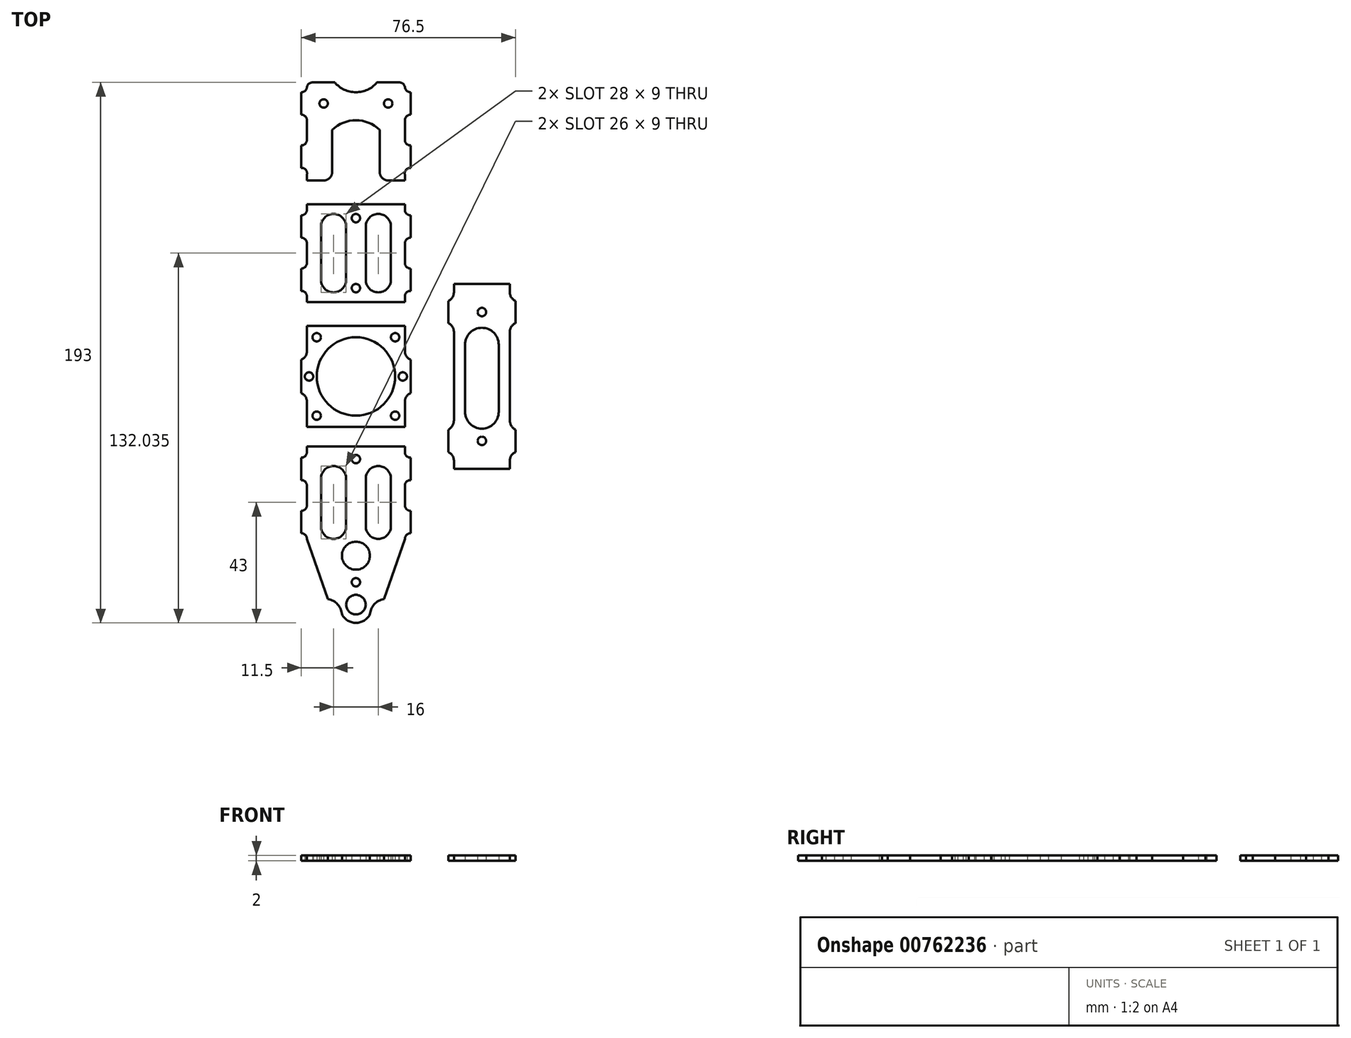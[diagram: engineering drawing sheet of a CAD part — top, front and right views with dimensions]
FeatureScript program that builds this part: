
annotation { "Feature Type Name" : "Feature", "Feature Type Description" : "" }
export const myFeature = defineFeature(function(context is Context, id is Id, definition is map)
    precondition{}
    {
        {
            var Q0;
            Q0=qCreatedBy(makeId("Top.planeOp"),FACE);
            var sketch = newSketch(context, id + "F0", { "sketchPlane" : qUnion([Q0])});
            skCircle(sketch, "E0", {"center": v(0, 0) * mm, "radius": 14 * mm});
            skCircle(sketch, "E1", {"center": v(-16.75, 0) * mm, "radius": 1.5 * mm});
            skLineSegment(sketch, "E2", {"start": v(-17.5, 18) * mm, "end": v(17.5, 18) * mm});
            skLineSegment(sketch, "E3.MirrorCS", {"start": v(-17.5, -18) * mm, "end": v(17.5, -18) * mm});
            skLineSegment(sketch, "E4", {"start": v(-17.5, 18) * mm, "end": v(-17.5, 9) * mm});
            skLineSegment(sketch, "E5", {"start": v(-19.5, 6) * mm, "end": v(-19.5, -6) * mm});
            skLineSegment(sketch, "E6.MirrorCS", {"start": v(-17.5, -18) * mm, "end": v(-17.5, -9) * mm});
            skLineSegment(sketch, "E7.MirrorCS", {"start": v(17.5, -18) * mm, "end": v(17.5, -9) * mm});
            skCircle(sketch, "E8.MirrorC", {"center": v(16.75, 0) * mm, "radius": 1.5 * mm});
            skLineSegment(sketch, "E9.MirrorCS", {"start": v(17.5, 18) * mm, "end": v(17.5, 9) * mm});
            skLineSegment(sketch, "E10.MirrorCS", {"start": v(19.5, 6) * mm, "end": v(19.5, -6) * mm});
            skCircle(sketch, "E11", {"center": v(-14, 14) * mm, "radius": 1.5 * mm});
            skCircle(sketch, "E12.MirrorC", {"center": v(-14, -14) * mm, "radius": 1.5 * mm});
            skCircle(sketch, "E13.MirrorC", {"center": v(14, 14) * mm, "radius": 1.5 * mm});
            skCircle(sketch, "E14.MirrorC", {"center": v(14, -14) * mm, "radius": 1.5 * mm});
            skArc(sketch, "E15", {"start": v(-19.5, 6) * mm, "mid": v(-18.05, 7.2) * mm, "end": v(-17.5, 9) * mm});
            skArc(sketch, "E16", {"start": v(17.5, 9) * mm, "mid": v(18.05, 7.2) * mm, "end": v(19.5, 6) * mm});
            skArc(sketch, "E17", {"start": v(-17.5, -9) * mm, "mid": v(-18.05, -7.2) * mm, "end": v(-19.5, -6) * mm});
            skArc(sketch, "E18", {"start": v(19.5, -6) * mm, "mid": v(18.05, -7.2) * mm, "end": v(17.5, -9) * mm});
            skSolve(sketch);
        }
        {
            var Q0;
            Q0 = qSketchRegion(id + "F0", true);
            extrude(context, id + "F1", {"entities" : qUnion([Q0]), "depth" : 2 * mm, "offsetDistance" : 25 * mm});
        }
        {
            var Q0;
            Q0=qCreatedBy(makeId("Top.planeOp"),FACE);
            var sketch = newSketch(context, id + "F2", { "sketchPlane" : qUnion([Q0])});
            skLineSegment(sketch, "E19", {"start": v(-17.5, 47.53) * mm, "end": v(-17.5, 40.53) * mm});
            skLineSegment(sketch, "E20", {"start": v(-17.5, 61.53) * mm, "end": v(17.5, 61.53) * mm});
            skPoint(sketch, "E21.positionSnap0", {"position": v(0, 61.53) * mm});
            skLineSegment(sketch, "E22", {"start": v(-17.5, 61.53) * mm, "end": v(-17.5, 59.53) * mm});
            skLineSegment(sketch, "E23", {"start": v(17.5, 47.53) * mm, "end": v(17.5, 40.53) * mm});
            skLineSegment(sketch, "E24", {"start": v(-17.5, 26.53) * mm, "end": v(17.5, 26.53) * mm});
            skPoint(sketch, "E25", {"position": v(0, 26.53) * mm});
            skLineSegment(sketch, "E26", {"start": v(-17.5, 28.53) * mm, "end": v(-17.5, 26.53) * mm});
            skLineSegment(sketch, "E27", {"start": v(-19.5, 57.53) * mm, "end": v(-19.5, 49.53) * mm});
            skLineSegment(sketch, "E28.MirrorCS", {"start": v(19.5, 57.53) * mm, "end": v(19.5, 49.53) * mm});
            skLineSegment(sketch, "E29", {"start": v(-19.5, 38.53) * mm, "end": v(-19.5, 30.53) * mm});
            skLineSegment(sketch, "E30", {"start": v(0, 61.53) * mm, "end": v(0, 26.53) * mm, "construction": true});
            skPoint(sketch, "E31", {"position": v(0, 44.03) * mm});
            skPoint(sketch, "E32", {"position": v(-17.5, 44.03) * mm});
            skPoint(sketch, "E33", {"position": v(17.5, 44.03) * mm});
            skLineSegment(sketch, "E34.MirrorCS", {"start": v(19.5, 38.53) * mm, "end": v(19.5, 30.53) * mm});
            skLineSegment(sketch, "E35", {"start": v(-17.5, 44.03) * mm, "end": v(17.5, 44.03) * mm, "construction": true});
            skLineSegment(sketch, "E36.MirrorCS", {"start": v(17.5, 61.53) * mm, "end": v(17.5, 59.53) * mm});
            skLineSegment(sketch, "E37.MirrorCS", {"start": v(17.5, 28.53) * mm, "end": v(17.5, 26.53) * mm});
            skArc(sketch, "E38", {"start": v(-17.5, 59.53) * mm, "mid": v(-18.09, 58.12) * mm, "end": v(-19.5, 57.53) * mm});
            skArc(sketch, "E39", {"start": v(-17.5, 47.53) * mm, "mid": v(-18.09, 48.95) * mm, "end": v(-19.5, 49.53) * mm});
            skArc(sketch, "E40.MirrorCS", {"start": v(-17.5, 28.53) * mm, "mid": v(-18.09, 29.95) * mm, "end": v(-19.5, 30.53) * mm});
            skArc(sketch, "E41.MirrorCS", {"start": v(-17.5, 40.53) * mm, "mid": v(-18.09, 39.12) * mm, "end": v(-19.5, 38.53) * mm});
            skArc(sketch, "E42.MirrorCS", {"start": v(17.5, 59.53) * mm, "mid": v(18.09, 58.12) * mm, "end": v(19.5, 57.53) * mm});
            skArc(sketch, "E43.MirrorCS", {"start": v(17.5, 47.53) * mm, "mid": v(18.09, 48.95) * mm, "end": v(19.5, 49.53) * mm});
            skArc(sketch, "E44.MirrorCS", {"start": v(17.5, 40.53) * mm, "mid": v(18.09, 39.12) * mm, "end": v(19.5, 38.53) * mm});
            skArc(sketch, "E45.MirrorCS", {"start": v(17.5, 28.53) * mm, "mid": v(18.09, 29.95) * mm, "end": v(19.5, 30.53) * mm});
            skLineSegment(sketch, "E46.top", {"start": v(-12.5, 34.53) * mm, "end": v(-3.5, 34.53) * mm, "construction": true});
            skLineSegment(sketch, "E46.left", {"start": v(-12.5, 53.53) * mm, "end": v(-12.5, 34.53) * mm});
            skLineSegment(sketch, "E46.right", {"start": v(-3.5, 53.53) * mm, "end": v(-3.5, 34.53) * mm});
            skArc(sketch, "E47", {"start": v(-3.5, 53.53) * mm, "mid": v(-8, 58.03) * mm, "end": v(-12.5, 53.53) * mm});
            skArc(sketch, "E48", {"start": v(-12.5, 34.53) * mm, "mid": v(-8, 30.03) * mm, "end": v(-3.5, 34.53) * mm});
            skLineSegment(sketch, "E49", {"start": v(-12.5, 53.53) * mm, "end": v(-3.5, 53.53) * mm, "construction": true});
            skLineSegment(sketch, "E50.MirrorCS", {"start": v(12.5, 34.53) * mm, "end": v(3.5, 34.53) * mm, "construction": true});
            skLineSegment(sketch, "E51.MirrorCS", {"start": v(12.5, 53.53) * mm, "end": v(3.5, 53.53) * mm, "construction": true});
            skArc(sketch, "E52.MirrorCS", {"start": v(12.5, 34.53) * mm, "mid": v(8, 30.03) * mm, "end": v(3.5, 34.53) * mm});
            skLineSegment(sketch, "E53.MirrorCS", {"start": v(12.5, 53.53) * mm, "end": v(12.5, 34.53) * mm});
            skLineSegment(sketch, "E54.MirrorCS", {"start": v(3.5, 53.53) * mm, "end": v(3.5, 34.53) * mm});
            skArc(sketch, "E55.MirrorCS", {"start": v(3.5, 53.53) * mm, "mid": v(8, 58.03) * mm, "end": v(12.5, 53.53) * mm});
            skPoint(sketch, "E56", {"position": v(-8, 58.03) * mm});
            skPoint(sketch, "E57", {"position": v(8, 58.03) * mm});
            skLineSegment(sketch, "E58", {"start": v(-8, 58.03) * mm, "end": v(8, 58.03) * mm, "construction": true});
            skCircle(sketch, "E59", {"center": v(0, 56.53) * mm, "radius": 1.5 * mm});
            skPoint(sketch, "E60", {"position": v(0, 58.03) * mm});
            skCircle(sketch, "E61.MirrorC", {"center": v(0, 31.53) * mm, "radius": 1.5 * mm});
            skSolve(sketch);
        }
        {
            var Q0;
            Q0 = qSketchRegion(id + "F2", true);
            extrude(context, id + "F3", {"entities" : qUnion([Q0]), "depth" : 2 * mm, "offsetDistance" : 25 * mm});
        }
        {
            var Q0;
            Q0=qCreatedBy(makeId("Top.planeOp"),FACE);
            var sketch = newSketch(context, id + "F4", { "sketchPlane" : qUnion([Q0])});
            skLineSegment(sketch, "E62", {"start": v(-17.5, 70) * mm, "end": v(-11.53, 70) * mm});
            skLineSegment(sketch, "E63", {"start": v(-17.5, 91.5) * mm, "end": v(-17.5, 84.5) * mm});
            skPoint(sketch, "E64", {"position": v(-17.5, 88) * mm});
            skLineSegment(sketch, "E65.MirrorCS", {"start": v(17.5, 91.5) * mm, "end": v(17.5, 84.5) * mm});
            skLineSegment(sketch, "E66", {"start": v(-17.5, 70) * mm, "end": v(-17.5, 72) * mm});
            skLineSegment(sketch, "E67.MirrorCS", {"start": v(17.5, 70) * mm, "end": v(11.53, 70) * mm});
            skLineSegment(sketch, "E68.MirrorCS", {"start": v(17.5, 70) * mm, "end": v(17.5, 72) * mm});
            skLineSegment(sketch, "E69", {"start": v(-8.5, 88) * mm, "end": v(-8.5, 73) * mm});
            skLineSegment(sketch, "E70.MirrorCS", {"start": v(8.5, 88) * mm, "end": v(8.5, 73) * mm});
            skArc(sketch, "E71", {"start": v(8.5, 88) * mm, "mid": v(0, 91.5) * mm, "end": v(-8.5, 88) * mm});
            skPoint(sketch, "E72", {"position": v(0, 91.5) * mm});
            skLineSegment(sketch, "E73", {"start": v(-15.53, 105) * mm, "end": v(-7.53, 105) * mm});
            skLineSegment(sketch, "E74", {"start": v(-17.52, 105) * mm, "end": v(-17.52, 101.5) * mm, "construction": true});
            skLineSegment(sketch, "E75.MirrorCS", {"start": v(15.53, 105) * mm, "end": v(7.53, 105) * mm});
            skLineSegment(sketch, "E76", {"start": v(-19.5, 101.5) * mm, "end": v(-19.5, 93.5) * mm});
            skLineSegment(sketch, "E77", {"start": v(-17.5, 88) * mm, "end": v(17.5, 88) * mm, "construction": true});
            skLineSegment(sketch, "E78.MirrorCS", {"start": v(-19.5, 74.5) * mm, "end": v(-19.5, 82.5) * mm});
            skArc(sketch, "E79", {"start": v(-17.5, 91.5) * mm, "mid": v(-18.09, 92.91) * mm, "end": v(-19.5, 93.5) * mm});
            skArc(sketch, "E80.MirrorCS", {"start": v(-17.5, 84.5) * mm, "mid": v(-18.09, 83.09) * mm, "end": v(-19.5, 82.5) * mm});
            skLineSegment(sketch, "E81", {"start": v(-19.5, 101.5) * mm, "end": v(-17.52, 101.5) * mm, "construction": true});
            skLineSegment(sketch, "E82", {"start": v(-17.52, 101.5) * mm, "end": v(-17.5, 70) * mm, "construction": true});
            skPoint(sketch, "E83", {"position": v(-17.52, 103.25) * mm});
            skArc(sketch, "E84", {"start": v(-19.5, 101.5) * mm, "mid": v(-18.18, 102) * mm, "end": v(-17.52, 103.25) * mm});
            skArc(sketch, "E85", {"start": v(-15.53, 105) * mm, "mid": v(-16.86, 104.5) * mm, "end": v(-17.52, 103.25) * mm});
            skLineSegment(sketch, "E86", {"start": v(0, 105) * mm, "end": v(0, 79.43) * mm, "construction": true});
            skPoint(sketch, "E87", {"position": v(0, 101.5) * mm});
            skArc(sketch, "E88", {"start": v(-7.53, 105) * mm, "mid": v(0, 101.5) * mm, "end": v(7.53, 105) * mm});
            skArc(sketch, "E89", {"start": v(-17.5, 72) * mm, "mid": v(-17.87, 73.75) * mm, "end": v(-19.5, 74.5) * mm});
            skPoint(sketch, "E90", {"position": v(-11.53, 105) * mm});
            skArc(sketch, "E91", {"start": v(-11.53, 70) * mm, "mid": v(-9.4, 70.87) * mm, "end": v(-8.5, 73) * mm});
            skArc(sketch, "E92.MirrorCS", {"start": v(11.53, 70) * mm, "mid": v(9.4, 70.87) * mm, "end": v(8.5, 73) * mm});
            skLineSegment(sketch, "E93.MirrorCS", {"start": v(19.5, 74.5) * mm, "end": v(19.5, 82.5) * mm});
            skLineSegment(sketch, "E94.MirrorCS", {"start": v(19.5, 101.5) * mm, "end": v(19.5, 93.5) * mm});
            skArc(sketch, "E95.MirrorCS", {"start": v(15.53, 105) * mm, "mid": v(16.86, 104.5) * mm, "end": v(17.52, 103.25) * mm});
            skArc(sketch, "E96.MirrorCS", {"start": v(19.5, 101.5) * mm, "mid": v(18.18, 102) * mm, "end": v(17.52, 103.25) * mm});
            skArc(sketch, "E97.MirrorCS", {"start": v(17.5, 91.5) * mm, "mid": v(18.09, 92.91) * mm, "end": v(19.5, 93.5) * mm});
            skArc(sketch, "E98.MirrorCS", {"start": v(17.5, 84.5) * mm, "mid": v(18.09, 83.09) * mm, "end": v(19.5, 82.5) * mm});
            skArc(sketch, "E99.MirrorCS", {"start": v(17.5, 72) * mm, "mid": v(17.87, 73.75) * mm, "end": v(19.5, 74.5) * mm});
            skPoint(sketch, "E100", {"position": v(-19.5, 97.5) * mm});
            skPoint(sketch, "E101.MirrorP", {"position": v(19.5, 97.5) * mm});
            skCircle(sketch, "E102", {"center": v(-11.53, 97.5) * mm, "radius": 1.5 * mm});
            skCircle(sketch, "E103.MirrorC", {"center": v(11.53, 97.5) * mm, "radius": 1.5 * mm});
            skSolve(sketch);
        }
        {
            var Q0;
            Q0 = qSketchRegion(id + "F4", true);
            extrude(context, id + "F5", {"entities" : qUnion([Q0]), "depth" : 2 * mm, "offsetDistance" : 25 * mm});
        }
        {
            var Q0;
            Q0=qCreatedBy(makeId("Top.planeOp"),FACE);
            var sketch = newSketch(context, id + "F6", { "sketchPlane" : qUnion([Q0])});
            skLineSegment(sketch, "E104", {"start": v(-17.5, -25) * mm, "end": v(17.5, -25) * mm});
            skPoint(sketch, "E105", {"position": v(0, -25) * mm});
            skCircle(sketch, "E106", {"center": v(0, -29.5) * mm, "radius": 1.5 * mm});
            skCircle(sketch, "E107", {"center": v(0, -64) * mm, "radius": 5 * mm});
            skCircle(sketch, "E108", {"center": v(0, -73.5) * mm, "radius": 1.5 * mm});
            skCircle(sketch, "E109", {"center": v(0, -81.5) * mm, "radius": 3.5 * mm});
            skPoint(sketch, "E110", {"position": v(0, -88) * mm});
            skPoint(sketch, "E111", {"position": v(0, -85) * mm});
            skLineSegment(sketch, "E112", {"start": v(-5, -85) * mm, "end": v(5, -85) * mm, "construction": true});
            skLineSegment(sketch, "E113", {"start": v(-10, -81.5) * mm, "end": v(10, -81.5) * mm, "construction": true});
            skLineSegment(sketch, "E114", {"start": v(-19.5, -29) * mm, "end": v(-19.5, -37) * mm});
            skLineSegment(sketch, "E115", {"start": v(-17.5, -25) * mm, "end": v(-17.5, -27) * mm});
            skArc(sketch, "E116", {"start": v(-19.5, -29) * mm, "mid": v(-18.09, -28.41) * mm, "end": v(-17.5, -27) * mm});
            skLineSegment(sketch, "E117", {"start": v(-17.5, -39) * mm, "end": v(-17.5, -46) * mm});
            skArc(sketch, "E118", {"start": v(-17.5, -39) * mm, "mid": v(-18.09, -37.59) * mm, "end": v(-19.5, -37) * mm});
            skPoint(sketch, "E119", {"position": v(-17.5, -42.5) * mm});
            skLineSegment(sketch, "E120", {"start": v(-17.5, -42.5) * mm, "end": v(17.5, -42.5) * mm, "construction": true});
            skLineSegment(sketch, "E121.MirrorCS", {"start": v(-19.5, -56) * mm, "end": v(-19.5, -48) * mm});
            skArc(sketch, "E122.MirrorCS", {"start": v(-19.5, -56) * mm, "mid": v(-18.09, -56.59) * mm, "end": v(-17.5, -58) * mm});
            skArc(sketch, "E123.MirrorCS", {"start": v(-17.5, -46) * mm, "mid": v(-18.09, -47.41) * mm, "end": v(-19.5, -48) * mm});
            skLineSegment(sketch, "E124.MirrorCS", {"start": v(17.5, -25) * mm, "end": v(17.5, -27) * mm});
            skArc(sketch, "E125.MirrorCS", {"start": v(19.5, -29) * mm, "mid": v(18.09, -28.41) * mm, "end": v(17.5, -27) * mm});
            skLineSegment(sketch, "E126.MirrorCS", {"start": v(19.5, -29) * mm, "end": v(19.5, -37) * mm});
            skArc(sketch, "E127.MirrorCS", {"start": v(17.5, -39) * mm, "mid": v(18.09, -37.59) * mm, "end": v(19.5, -37) * mm});
            skLineSegment(sketch, "E128.MirrorCS", {"start": v(17.5, -39) * mm, "end": v(17.5, -46) * mm});
            skArc(sketch, "E129.MirrorCS", {"start": v(17.5, -46) * mm, "mid": v(18.09, -47.41) * mm, "end": v(19.5, -48) * mm});
            skLineSegment(sketch, "E130.MirrorCS", {"start": v(19.5, -56) * mm, "end": v(19.5, -48) * mm});
            skArc(sketch, "E131.MirrorCS", {"start": v(19.5, -56) * mm, "mid": v(18.09, -56.59) * mm, "end": v(17.5, -58) * mm});
            skArc(sketch, "E132", {"start": v(-8, -81.5) * mm, "mid": v(-8.59, -80.09) * mm, "end": v(-10, -79.5) * mm, "construction": true});
            skArc(sketch, "E133.MirrorCS", {"start": v(8, -81.5) * mm, "mid": v(8.59, -80.09) * mm, "end": v(10, -79.5) * mm, "construction": true});
            skLineSegment(sketch, "E134", {"start": v(-17.5, -58) * mm, "end": v(-10, -79.5) * mm});
            skArc(sketch, "E135", {"start": v(-5, -85) * mm, "mid": v(-5.84, -82.69) * mm, "end": v(-8, -81.5) * mm, "construction": true});
            skArc(sketch, "E136", {"start": v(-5, -85) * mm, "mid": v(-6.55, -81.38) * mm, "end": v(-10, -79.5) * mm});
            skArc(sketch, "E137", {"start": v(-5, -85) * mm, "mid": v(0, -88) * mm, "end": v(5, -85) * mm});
            skLineSegment(sketch, "E138.MirrorCS", {"start": v(17.5, -58) * mm, "end": v(10, -79.5) * mm});
            skArc(sketch, "E139.MirrorCS", {"start": v(5, -85) * mm, "mid": v(6.55, -81.38) * mm, "end": v(10, -79.5) * mm});
            skLineSegment(sketch, "E140.bottom", {"start": v(-12.5, -36.5) * mm, "end": v(-3.5, -36.5) * mm, "construction": true});
            skLineSegment(sketch, "E140.top", {"start": v(-12.5, -53.5) * mm, "end": v(-3.5, -53.5) * mm, "construction": true});
            skLineSegment(sketch, "E140.left", {"start": v(-12.5, -36.5) * mm, "end": v(-12.5, -53.5) * mm});
            skLineSegment(sketch, "E140.right", {"start": v(-3.5, -36.5) * mm, "end": v(-3.5, -53.5) * mm});
            skArc(sketch, "E141", {"start": v(-3.5, -36.5) * mm, "mid": v(-8, -32) * mm, "end": v(-12.5, -36.5) * mm});
            skArc(sketch, "E142", {"start": v(-12.5, -53.5) * mm, "mid": v(-8, -58) * mm, "end": v(-3.5, -53.5) * mm});
            skLineSegment(sketch, "E143.MirrorCS", {"start": v(3.5, -36.5) * mm, "end": v(3.5, -53.5) * mm});
            skArc(sketch, "E144.MirrorCS", {"start": v(3.5, -36.5) * mm, "mid": v(8, -32) * mm, "end": v(12.5, -36.5) * mm});
            skArc(sketch, "E145.MirrorCS", {"start": v(12.5, -53.5) * mm, "mid": v(8, -58) * mm, "end": v(3.5, -53.5) * mm});
            skLineSegment(sketch, "E146.MirrorCS", {"start": v(12.5, -36.5) * mm, "end": v(12.5, -53.5) * mm});
            skPoint(sketch, "E147", {"position": v(-19.5, -33) * mm});
            skPoint(sketch, "E148", {"position": v(-19.5, -52) * mm});
            skSolve(sketch);
        }
        {
            var Q0;
            Q0 = qSketchRegion(id + "F6", true);
            extrude(context, id + "F7", {"entities" : qUnion([Q0]), "depth" : 2 * mm, "offsetDistance" : 25 * mm});
        }
        {
            var Q0;
            Q0=qCreatedBy(makeId("Top.planeOp"),FACE);
            var sketch = newSketch(context, id + "F8", { "sketchPlane" : qUnion([Q0])});
            skLineSegment(sketch, "E149", {"start": v(35, 33) * mm, "end": v(55, 33) * mm});
            skLineSegment(sketch, "E150.MirrorCS", {"start": v(35, -33) * mm, "end": v(55, -33) * mm});
            skPoint(sketch, "E151", {"position": v(45, 33) * mm});
            skLineSegment(sketch, "E152", {"start": v(45, 33) * mm, "end": v(45, -33) * mm, "construction": true});
            skLineSegment(sketch, "E153", {"start": v(35, 16) * mm, "end": v(35, -15.68) * mm});
            skLineSegment(sketch, "E154.MirrorCS", {"start": v(55, 16) * mm, "end": v(55, -15.68) * mm});
            skPoint(sketch, "E155", {"position": v(45, 0) * mm});
            skLineSegment(sketch, "E156", {"start": v(33, 27) * mm, "end": v(33, 19) * mm});
            skLineSegment(sketch, "E157.MirrorCS", {"start": v(57, 27) * mm, "end": v(57, 19) * mm});
            skLineSegment(sketch, "E158", {"start": v(35, 33) * mm, "end": v(35, 30) * mm});
            skPoint(sketch, "E159", {"position": v(33, 23) * mm});
            skLineSegment(sketch, "E160", {"start": v(33, 23) * mm, "end": v(57, 23) * mm, "construction": true});
            skLineSegment(sketch, "E161.MirrorCS", {"start": v(35, -33) * mm, "end": v(35, -30) * mm});
            skLineSegment(sketch, "E162.MirrorCS", {"start": v(33, -27) * mm, "end": v(33, -19) * mm});
            skLineSegment(sketch, "E163.MirrorCS", {"start": v(55, 33) * mm, "end": v(55, 30) * mm});
            skLineSegment(sketch, "E164.MirrorCS", {"start": v(57, -27) * mm, "end": v(57, -19) * mm});
            skLineSegment(sketch, "E165.MirrorCS", {"start": v(55, -33) * mm, "end": v(55, -30) * mm});
            skCircle(sketch, "E166", {"center": v(45, 23) * mm, "radius": 1.5 * mm});
            skCircle(sketch, "E167.MirrorC", {"center": v(45, -23) * mm, "radius": 1.5 * mm});
            skLineSegment(sketch, "E168.bottom", {"start": v(39, 11.38) * mm, "end": v(51, 11.38) * mm, "construction": true});
            skLineSegment(sketch, "E168.top", {"start": v(39, -12.62) * mm, "end": v(51, -12.62) * mm, "construction": true});
            skLineSegment(sketch, "E168.left", {"start": v(39, 11.38) * mm, "end": v(39, -12.62) * mm});
            skLineSegment(sketch, "E168.right", {"start": v(51, 11.38) * mm, "end": v(51, -12.62) * mm});
            skArc(sketch, "E169", {"start": v(51, 11.38) * mm, "mid": v(45, 17.38) * mm, "end": v(39, 11.38) * mm});
            skArc(sketch, "E170", {"start": v(39, -12.62) * mm, "mid": v(45, -18.62) * mm, "end": v(51, -12.62) * mm});
            skArc(sketch, "E171", {"start": v(35, -30) * mm, "mid": v(34.45, -28.2) * mm, "end": v(33, -27) * mm});
            skArc(sketch, "E172", {"start": v(33, -19) * mm, "mid": v(34.46, -17.62) * mm, "end": v(35, -15.68) * mm});
            skArc(sketch, "E173", {"start": v(57, -27) * mm, "mid": v(55.55, -28.2) * mm, "end": v(55, -30) * mm});
            skArc(sketch, "E174", {"start": v(55, -15.68) * mm, "mid": v(55.54, -17.62) * mm, "end": v(57, -19) * mm});
            skArc(sketch, "E175", {"start": v(35, 16) * mm, "mid": v(34.45, 17.8) * mm, "end": v(33, 19) * mm});
            skArc(sketch, "E176", {"start": v(33, 27) * mm, "mid": v(34.45, 28.2) * mm, "end": v(35, 30) * mm});
            skArc(sketch, "E177", {"start": v(57, 19) * mm, "mid": v(55.55, 17.8) * mm, "end": v(55, 16) * mm});
            skArc(sketch, "E178", {"start": v(55, 30) * mm, "mid": v(55.55, 28.2) * mm, "end": v(57, 27) * mm});
            skPoint(sketch, "E179", {"position": v(33, -23) * mm});
            skSolve(sketch);
        }
        {
            var Q0;
            Q0 = qSketchRegion(id + "F8", true);
            extrude(context, id + "F9", {"entities" : qUnion([Q0]), "depth" : 2 * mm, "offsetDistance" : 25 * mm});
        }
    });
